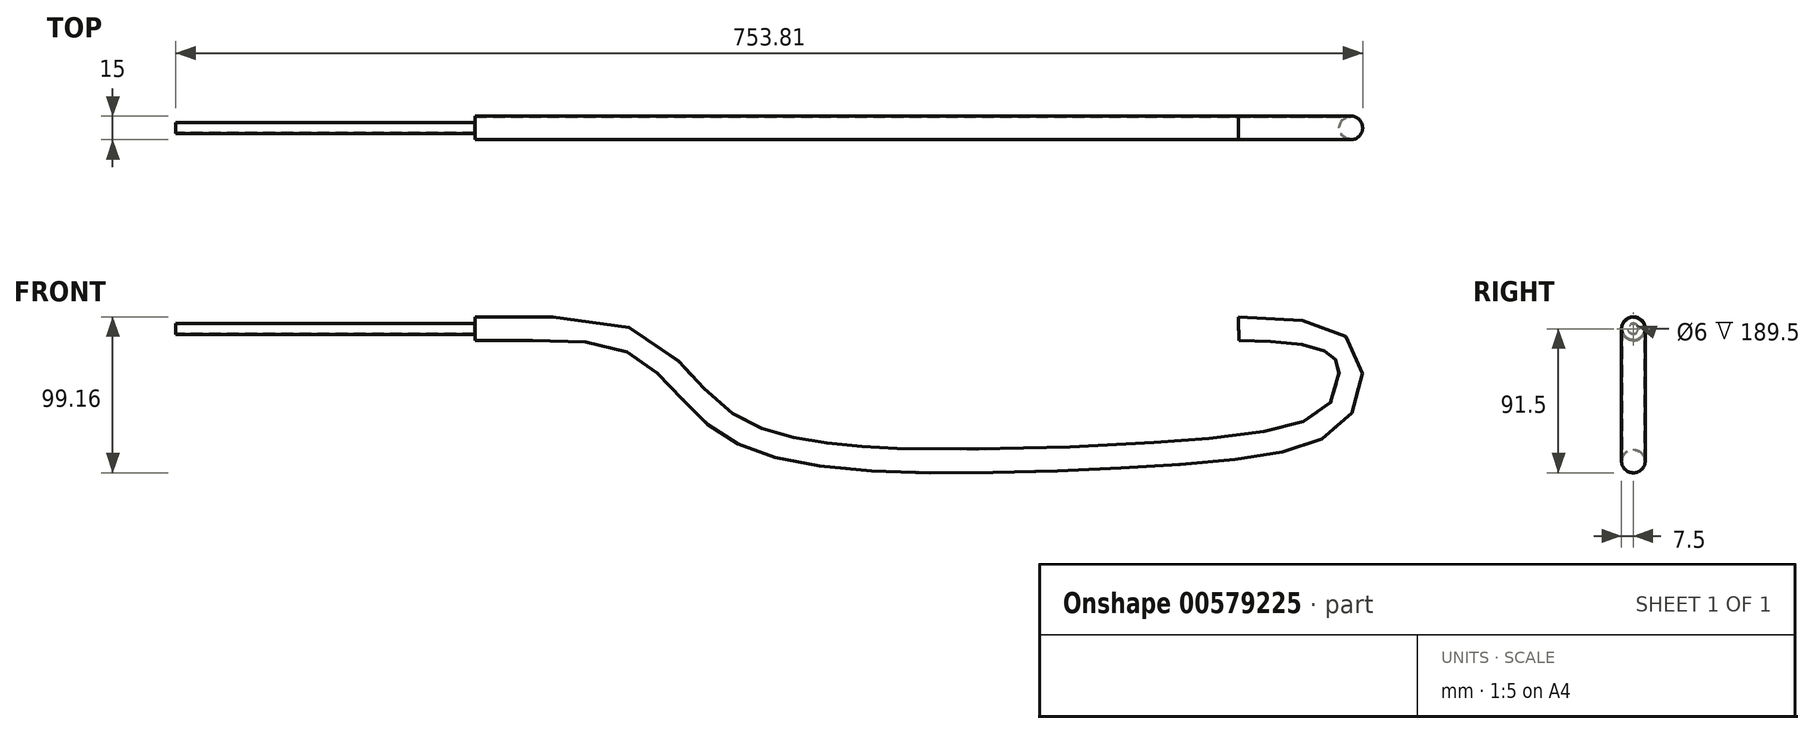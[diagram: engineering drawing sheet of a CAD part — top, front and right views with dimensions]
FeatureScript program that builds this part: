
annotation { "Feature Type Name" : "Feature", "Feature Type Description" : "" }
export const myFeature = defineFeature(function(context is Context, id is Id, definition is map)
    precondition{}
    {
        {
            var Q0;
            Q0=qCreatedBy(makeId("Right.planeOp"),FACE);
            var sketch = newSketch(context, id + "F0", { "sketchPlane" : qUnion([Q0])});
            skCircle(sketch, "E0", {"center": v(0, 0) * mm, "radius": 7.5 * mm});
            skCircle(sketch, "E1", {"center": v(0, 0) * mm, "radius": 7 * mm});
            skSolve(sketch);
        }
        {
            var Q0;
            Q0=qCreatedBy(makeId("Front.planeOp"),FACE);
            var sketch = newSketch(context, id + "F1", { "sketchPlane" : qUnion([Q0])});
            skFitSpline(sketch, "E2", {"points": [v(0, 0) * mm, v(93.26, -5.3) * mm, v(133.7, -36.17) * mm, v(161.51, -61.41) * mm, v(203.74, -77.03) * mm, v(296.87, -83.97) * mm, v(427.6, -79.92) * mm, v(514.36, -70.09) * mm, v(549.8, -50.72) * mm, v(553.36, -16.74) * mm, v(485.02, 0) * mm], "startDerivative": vector(824.21, -24.96) * mm, "endDerivative": vector(-1091.73, 0) * mm});
            skSolve(sketch);
        }
        {
            var Q0;
            Q0=makeQuery(id+"F0.imprint","IMPRINT",FACE,{"disambiguationData":[TD([[makeQuery(id+"F0.imprint","IMPRINT",EDGE,{"derivedFrom":sQuery(id+"F0.wireOp",EDGE,"E0")}),1.0]])]});
            var Q1;
            Q1=sQuery(id+"F1.wireOp",EDGE,"E2");
            sweep(context, id + "F2", {"profiles" : qUnion([Q0]), "path" : qUnion([Q1])});
        }
        {
            var Q0;
            Q0=qCreatedBy(makeId("Right.planeOp"),FACE);
            var sketch = newSketch(context, id + "F3", { "sketchPlane" : qUnion([Q0])});
            skCircle(sketch, "E3", {"center": v(0, 0) * mm, "radius": 3.5 * mm});
            skSolve(sketch);
        }
        {
            var Q0;
            Q0=qCreatedBy(makeId("Front.planeOp"),FACE);
            var sketch = newSketch(context, id + "F4", { "sketchPlane" : qUnion([Q0])});
            skLineSegment(sketch, "E4", {"start": v(0, 0) * mm, "end": v(-190, 0) * mm});
            skSolve(sketch);
        }
        {
            var Q0;
            Q0=makeQuery(id+"F3.imprint","IMPRINT",FACE,{"disambiguationData":[TD([[makeQuery(id+"F3.imprint","IMPRINT",EDGE,{"derivedFrom":sQuery(id+"F3.wireOp",EDGE,"E3")}),1.0]])]});
            var Q1;
            Q1=sQuery(id+"F4.wireOp",EDGE,"E4");
            sweep(context, id + "F5", {"profiles" : qUnion([Q0]), "path" : qUnion([Q1])});
        }
        {
            var Q0;
            Q0=makeQuery(id+"F5.opSweep","CAP_FACE",FACE,{"disambiguationData":[OSD([sQuery(id+"F3.wireOp",EDGE,"E3"),sQuery(id+"F4.wireOp",VERTEX,"E4.end")])],"isStart":false});
            shell(context, id + "F6", {"entities" : qUnion([Q0]), "thickness" : 0.5 * mm});
        }
    });
